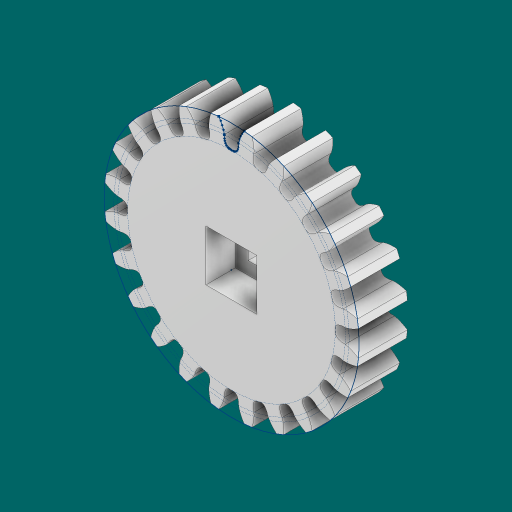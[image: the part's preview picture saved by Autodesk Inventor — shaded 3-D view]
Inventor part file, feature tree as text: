
AUTODESK INVENTOR PART (.ipt)
format: ipt  version: 2023.1 (Build 271208000, 208)  size: 729,088 bytes
history: native  units: in
note: dims shown in document units (in); Inventor stores cm internally (conversion verified against a paired STEP export)
features: extrude x4, sketch x3, pattern_circular x1
ambient origin geometry x8: Origin, YZ Plane, XZ Plane, XY Plane, X Axis, Y Axis, Z Axis, Center Point
bodies: Solid1 (feature_tree)
feature tree (8):
  sketch  "Sketch1"  dims[d0=0.25in d1=0.0in]
  extrude  "Extrusion1"  TaperAngle=0.0deg  [1 undecoded]
  extrude  "Extrusion2"  Depth=9.4488in TaperAngle=360.0deg
  pattern_circular  "Circular Pattern1"  [2 undecoded]
  extrude  "Extrusion3"  Depth=0.15in TaperAngle=0.0deg
  extrude  "Extrusion4"  Depth=0.13in
  sketch  "Sketch2"  dims[d2=0.0in d3=0.0in d4=9.4488in d5=360.0deg]
  sketch  "Sketch3"  dims[d7=0.26in d8=0.26in d9=0.15in d10=0.0in d11=0.13in d12=0.13in d13=0.0in d14=0.0in]
note: 3 required parameter values undecoded (feature->parameter linkage not recoverable at this tier; creation-order binding heuristic only, values carry confidence <= 0.55)
